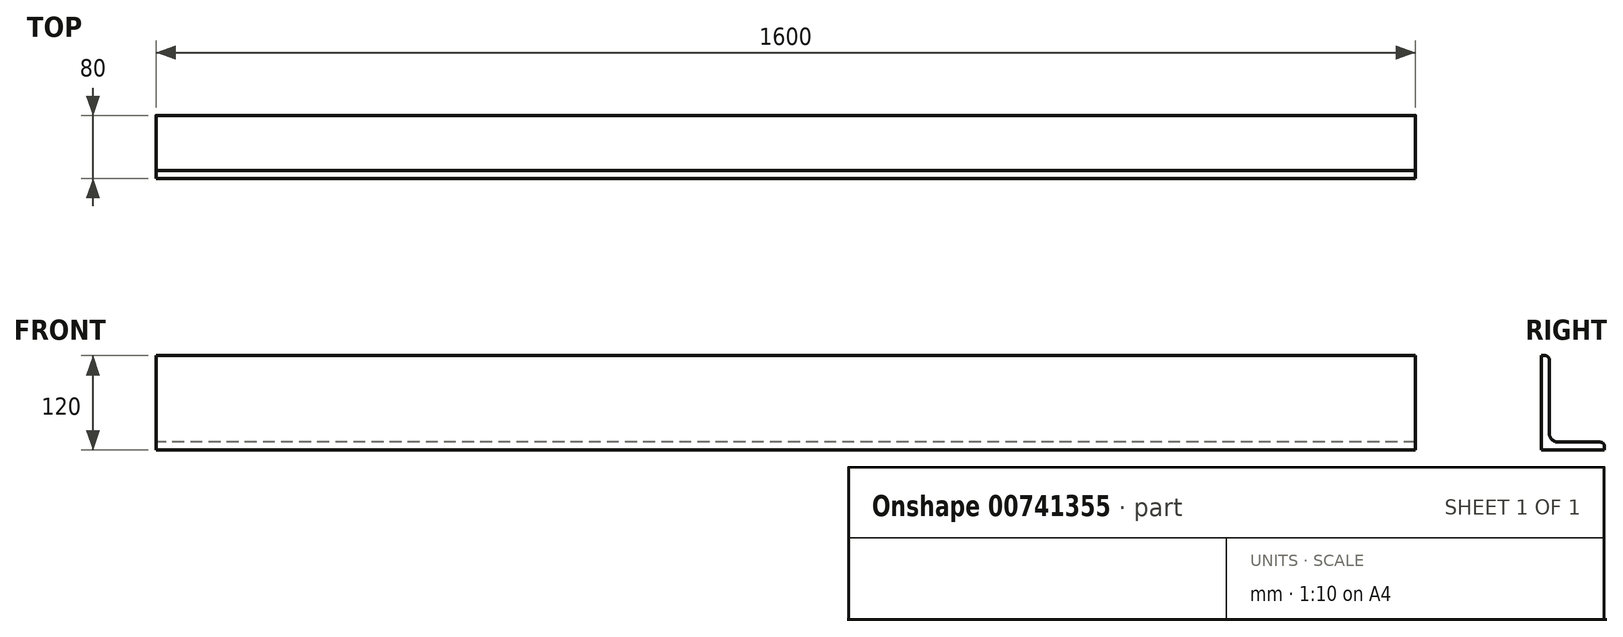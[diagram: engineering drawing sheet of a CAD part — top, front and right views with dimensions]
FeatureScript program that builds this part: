
annotation { "Feature Type Name" : "Feature", "Feature Type Description" : "" }
export const myFeature = defineFeature(function(context is Context, id is Id, definition is map)
    precondition{}
    {
        {
            var Q0;
            Q0=qCreatedBy(makeId("Right.planeOp"),FACE);
            var sketch = newSketch(context, id + "F0", { "sketchPlane" : qUnion([Q0])});
            skLineSegment(sketch, "E0", {"start": v(0, 0) * mm, "end": v(0, 120) * mm});
            skLineSegment(sketch, "E1", {"start": v(0, 0) * mm, "end": v(80, 0) * mm});
            skLineSegment(sketch, "E2", {"start": v(80, 0) * mm, "end": v(80, 4.5) * mm});
            skLineSegment(sketch, "E3", {"start": v(74.5, 10) * mm, "end": v(21, 10) * mm});
            skLineSegment(sketch, "E4", {"start": v(10, 21) * mm, "end": v(10, 114.5) * mm});
            skLineSegment(sketch, "E5", {"start": v(4.5, 120) * mm, "end": v(0, 120) * mm});
            skPoint(sketch, "E6.visualSharp", {"position": v(10, 120) * mm});
            skArc(sketch, "E6.filletArc", {"start": v(10, 114.5) * mm, "mid": v(8.39, 118.39) * mm, "end": v(4.5, 120) * mm});
            skPoint(sketch, "E7.visualSharp", {"position": v(80, 10) * mm});
            skArc(sketch, "E7.filletArc", {"start": v(80, 4.5) * mm, "mid": v(78.39, 8.39) * mm, "end": v(74.5, 10) * mm});
            skPoint(sketch, "E8.visualSharp", {"position": v(10, 10) * mm});
            skArc(sketch, "E8.filletArc", {"start": v(10, 21) * mm, "mid": v(13.22, 13.22) * mm, "end": v(21, 10) * mm});
            skSolve(sketch);
        }
        {
            var Q0;
            Q0=makeQuery(id+"F0.imprint","IMPRINT",FACE,{"disambiguationData":[TD([[makeQuery(id+"F0.imprint","IMPRINT",EDGE,{"derivedFrom":sQuery(id+"F0.wireOp",EDGE,"E0")}),-1.0]])]});
            extrude(context, id + "F1", {"entities" : qUnion([Q0]), "endBound" : BoundingType.SYMMETRIC, "depth" : 1600 * mm, "offsetDistance" : 25 * mm});
        }
    });
